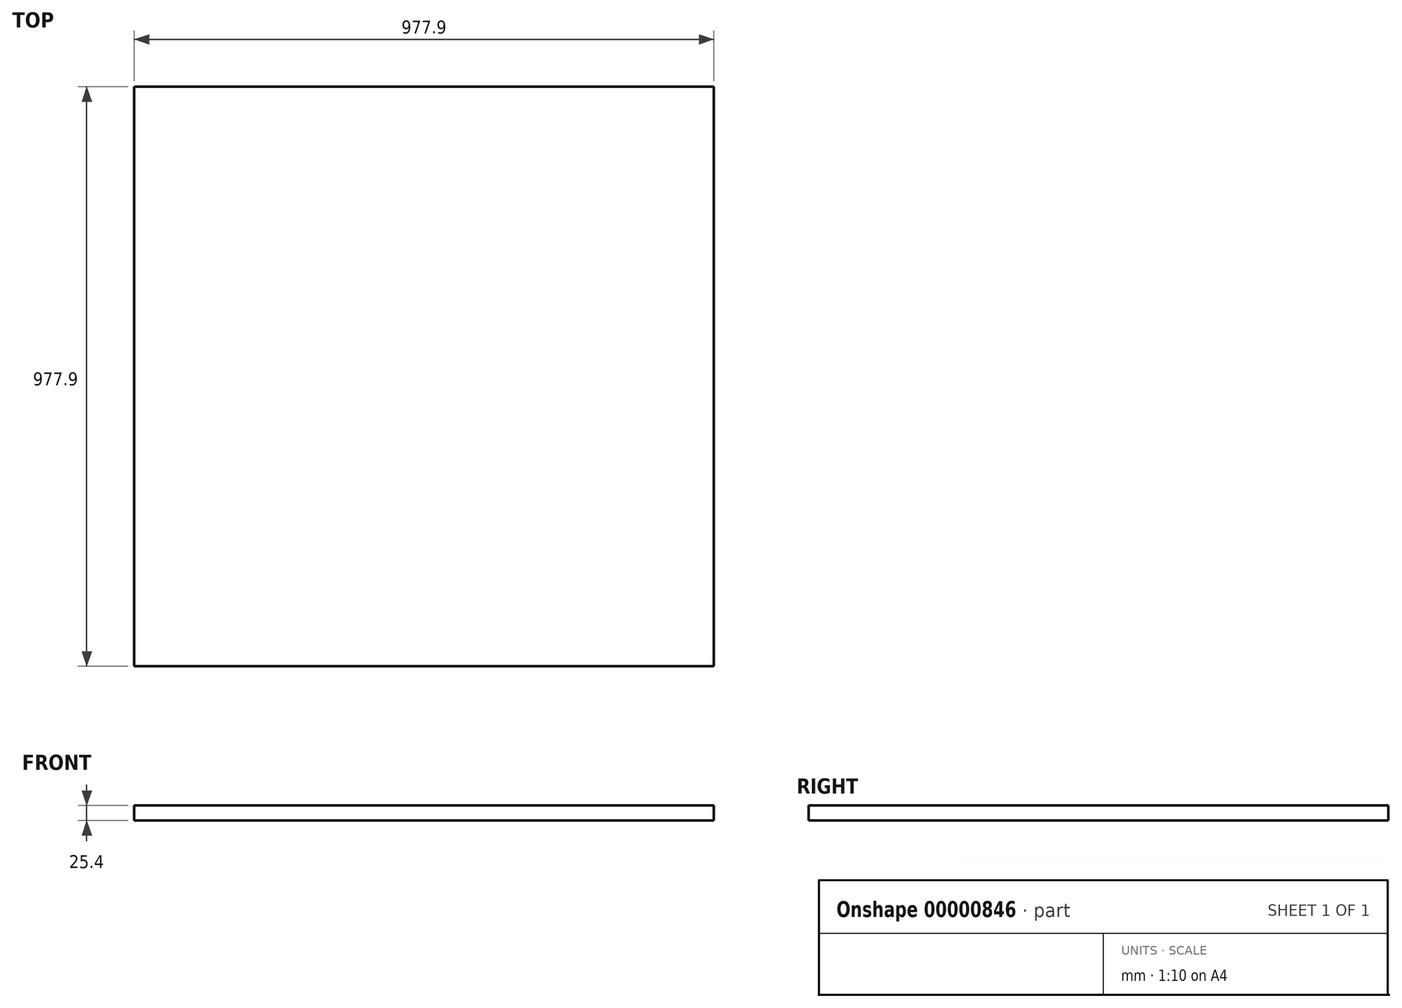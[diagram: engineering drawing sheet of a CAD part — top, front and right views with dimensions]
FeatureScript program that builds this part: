
annotation { "Feature Type Name" : "Feature", "Feature Type Description" : "" }
export const myFeature = defineFeature(function(context is Context, id is Id, definition is map)
    precondition{}
    {
        {
            var Q0;
            Q0=qCreatedBy(makeId("Front.planeOp"),FACE);
            var sketch = newSketch(context, id + "F0", { "sketchPlane" : qUnion([Q0])});
            skLineSegment(sketch, "E0", {"start": v(-488.95, 0) * mm, "end": v(488.95, 0) * mm});
            skLineSegment(sketch, "E1", {"start": v(488.95, 0) * mm, "end": v(488.95, 25.4) * mm});
            skLineSegment(sketch, "E2", {"start": v(488.95, 25.4) * mm, "end": v(-488.95, 25.4) * mm});
            skLineSegment(sketch, "E3", {"start": v(-488.95, 25.4) * mm, "end": v(-488.95, 0) * mm});
            skLineSegment(sketch, "E4", {"start": v(0, 112.64) * mm, "end": v(0, -139.92) * mm, "construction": true});
            skLineSegment(sketch, "E5", {"start": v(-563.63, 0) * mm, "end": v(563.95, 0) * mm, "construction": true});
            skSolve(sketch);
        }
        {
            var Q0;
            Q0 = qSketchRegion(id + "F0", true);
            extrude(context, id + "F1", {"entities" : qUnion([Q0]), "oppositeDirection" : true, "depth" : 977.9 * mm});
        }
    });
